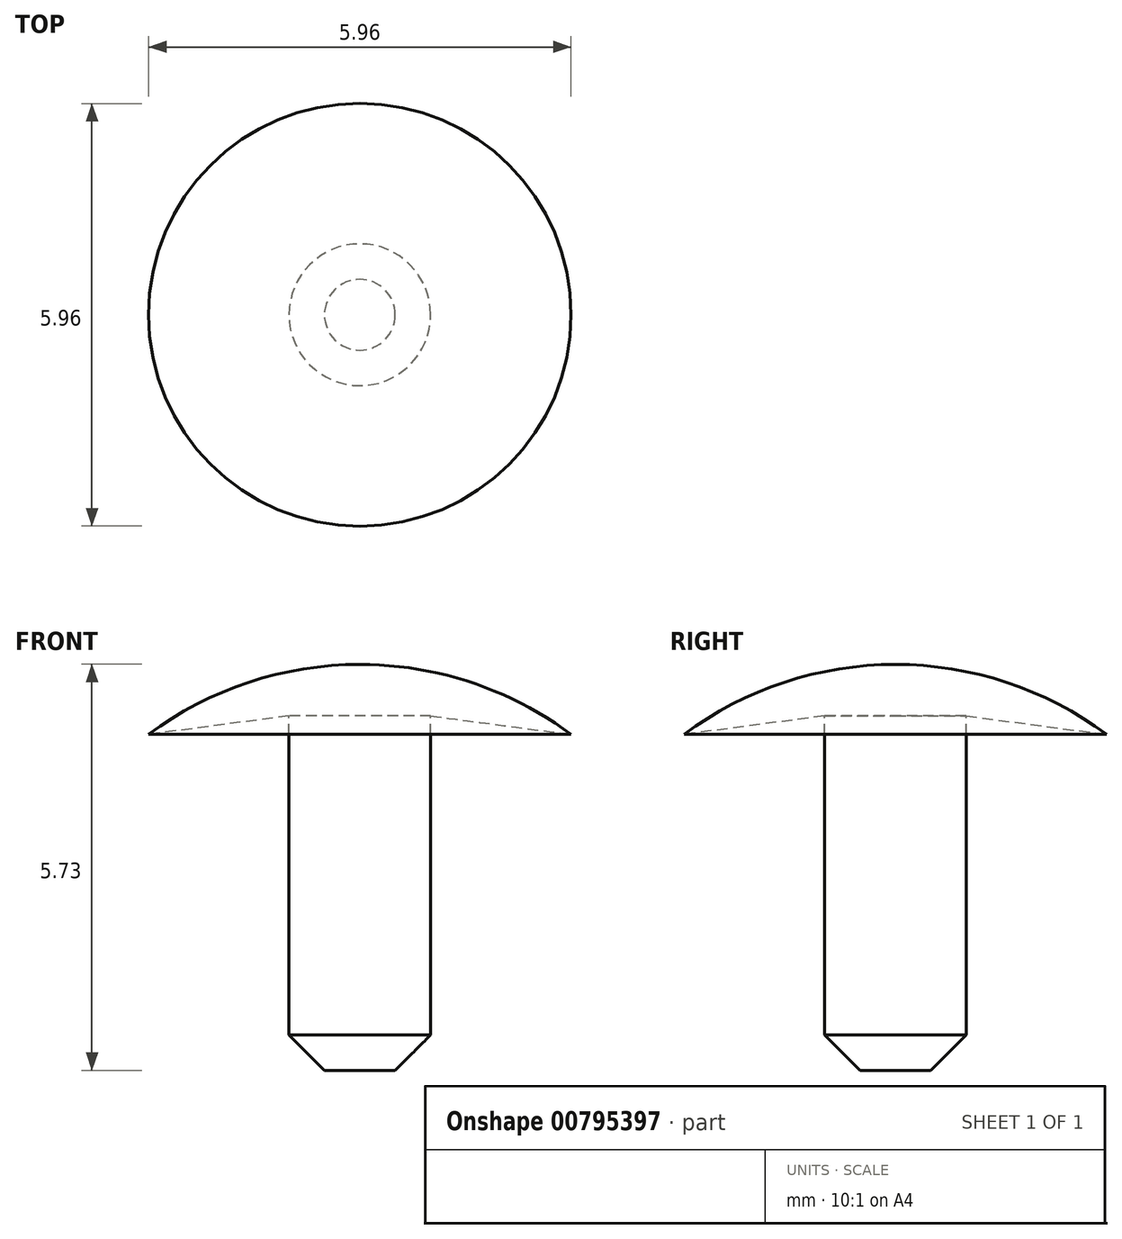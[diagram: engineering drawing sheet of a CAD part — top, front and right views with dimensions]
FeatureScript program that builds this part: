
annotation { "Feature Type Name" : "Feature", "Feature Type Description" : "" }
export const myFeature = defineFeature(function(context is Context, id is Id, definition is map)
    precondition{}
    {
        {
            var Q0;
            Q0=qCreatedBy(makeId("Front.planeOp"),FACE);
            var sketch = newSketch(context, id + "F0", { "sketchPlane" : qUnion([Q0])});
            skLineSegment(sketch, "E0", {"start": v(0, 0) * mm, "end": v(-1, 0) * mm});
            skLineSegment(sketch, "E1", {"start": v(-1, 0) * mm, "end": v(-1, 5) * mm});
            skLineSegment(sketch, "E2", {"start": v(-1, 5) * mm, "end": v(-2.98, 4.74) * mm});
            skArc(sketch, "E3", {"start": v(0, 5.73) * mm, "mid": v(-1.57, 5.47) * mm, "end": v(-2.98, 4.74) * mm});
            skLineSegment(sketch, "E4", {"start": v(0, 5.73) * mm, "end": v(0, 0) * mm});
            skSolve(sketch);
        }
        {
            var Q0;
            Q0 = qSketchRegion(id + "F0", true);
            var Q1;
            Q1=sQuery(id+"F0.wireOp",EDGE,"E4");
            revolve(context, id + "F1", {"surfaceOperationType" : NewSurfaceOperationType.NEW, "entities" : qUnion([Q0]), "axis" : qUnion([Q1]), "revolveType" : RevolveType.FULL});
        }
        {
            var Q0;
            Q0=makeQuery(id+"F1.opRevolve","SWEPT_EDGE",EDGE,{"disambiguationData":[OSD([sQuery(id+"F0.wireOp",EDGE,"E0"),sQuery(id+"F0.wireOp",EDGE,"E1")])]});
            chamfer(context, id + "F2", {"entities" : qUnion([Q0]), "width" : .5 * mm, "tangentPropagation" : true});
        }
    });
